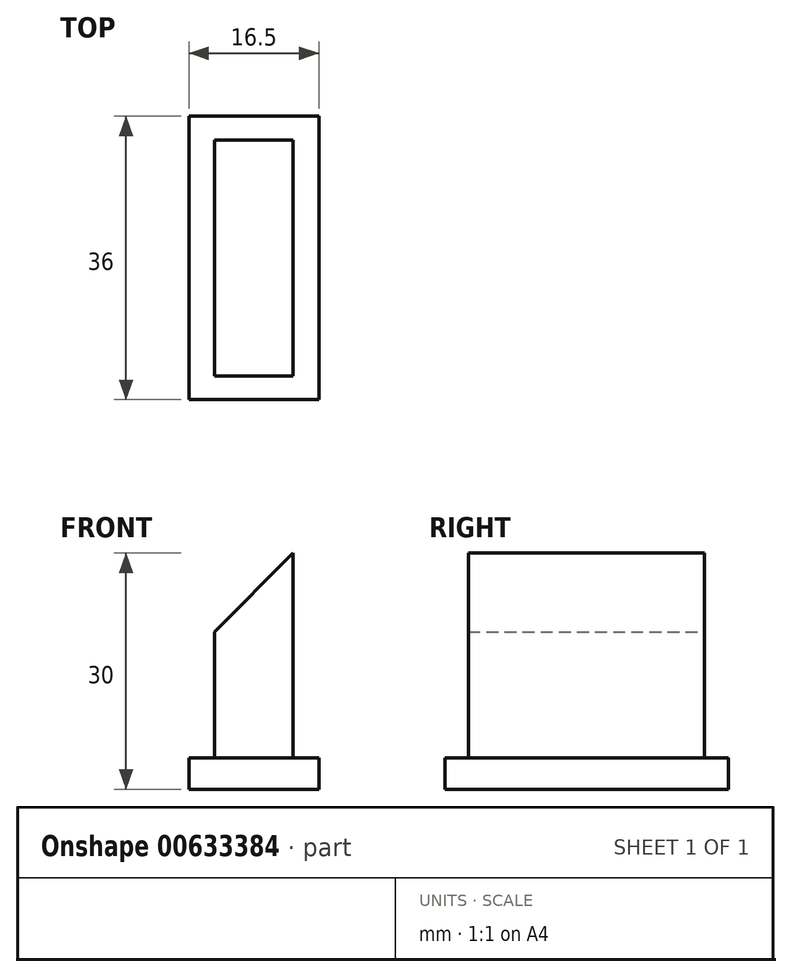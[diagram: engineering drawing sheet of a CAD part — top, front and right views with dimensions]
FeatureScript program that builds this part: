
annotation { "Feature Type Name" : "Feature", "Feature Type Description" : "" }
export const myFeature = defineFeature(function(context is Context, id is Id, definition is map)
    precondition{}
    {
        {
            var Q0;
            Q0=qCreatedBy(makeId("Top.planeOp"),FACE);
            var sketch = newSketch(context, id + "F0", { "sketchPlane" : qUnion([Q0])});
            skLineSegment(sketch, "E0.bottom", {"start": v(0, 0) * mm, "end": v(16.5, 0) * mm});
            skLineSegment(sketch, "E0.top", {"start": v(0, 36) * mm, "end": v(16.5, 36) * mm});
            skLineSegment(sketch, "E0.left", {"start": v(0, 0) * mm, "end": v(0, 36) * mm});
            skLineSegment(sketch, "E0.right", {"start": v(16.5, 0) * mm, "end": v(16.5, 36) * mm});
            skSolve(sketch);
        }
        {
            var Q0;
            Q0=qSketchRegion(id+"F0",true);
            extrude(context, id + "F1", {"entities" : qUnion([Q0]), "depth" : 4 * mm, "offsetDistance" : 25 * mm});
        }
        {
            var Q0;
            Q0=qCreatedBy(makeId("Top.planeOp"),FACE);
            var sketch = newSketch(context, id + "F2", { "sketchPlane" : qUnion([Q0])});
            skLineSegment(sketch, "E1.bottom", {"start": v(3.25, 33) * mm, "end": v(13.25, 33) * mm});
            skLineSegment(sketch, "E1.top", {"start": v(3.25, 3) * mm, "end": v(13.25, 3) * mm});
            skLineSegment(sketch, "E1.left", {"start": v(3.25, 33) * mm, "end": v(3.25, 3) * mm});
            skLineSegment(sketch, "E1.right", {"start": v(13.25, 33) * mm, "end": v(13.25, 3) * mm});
            skSolve(sketch);
        }
        {
            var Q0;
            Q0=qSketchRegion(id+"F2",true);
            extrude(context, id + "F3", {"entities" : qUnion([Q0]), "operationType" : NewBodyOperationType.ADD, "depth" : 30 * mm, "offsetDistance" : 25 * mm});
        }
        {
            var Q0;
            Q0=makeQuery(id+"F3.opExtrude","CAP_EDGE",EDGE,{"disambiguationData":[OSD([sQuery(id+"F2.wireOp",EDGE,"E1.left")])],"isStart":false});
            chamfer(context, id + "F4", {"entities" : qUnion([Q0]), "width" : 10 * mm, "tangentPropagation" : true});
        }
    });
